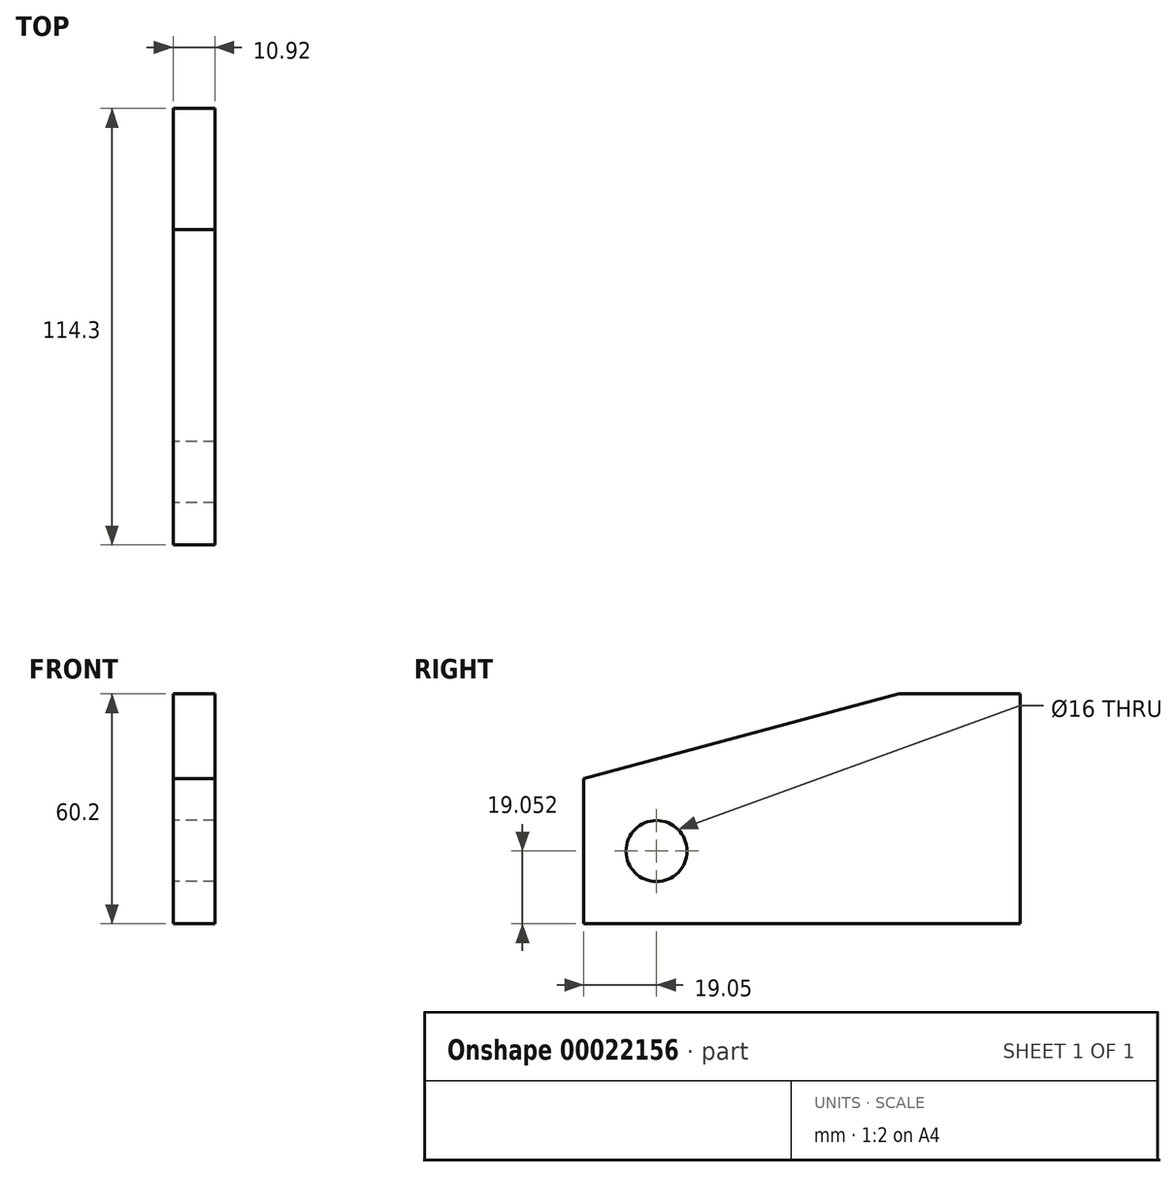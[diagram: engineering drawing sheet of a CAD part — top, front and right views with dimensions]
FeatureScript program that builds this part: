
annotation { "Feature Type Name" : "Feature", "Feature Type Description" : "" }
export const myFeature = defineFeature(function(context is Context, id is Id, definition is map)
    precondition{}
    {
        {
            var Q0;
            Q0=qCreatedBy(makeId("Right.planeOp"),FACE);
            var sketch = newSketch(context, id + "F0", { "sketchPlane" : qUnion([Q0])});
            skLineSegment(sketch, "E0.bottom", {"start": v(82.55, 0) * mm, "end": v(114.3, 0) * mm});
            skLineSegment(sketch, "E0.top", {"start": v(0, -60.2) * mm, "end": v(114.3, -60.2) * mm});
            skLineSegment(sketch, "E0.left", {"start": v(0, -22.12) * mm, "end": v(0, -60.2) * mm});
            skLineSegment(sketch, "E0.right", {"start": v(114.3, 0) * mm, "end": v(114.3, -60.2) * mm});
            skLineSegment(sketch, "E1", {"start": v(82.55, 0) * mm, "end": v(0, -22.12) * mm});
            skCircle(sketch, "E2", {"center": v(19.05, -41.15) * mm, "radius": 8 * mm});
            skSolve(sketch);
        }
        {
            var Q0;
            Q0 = qSketchRegion(id + "F0", true);
            extrude(context, id + "F1", {"entities" : qUnion([Q0]), "depth" : 10.92 * mm});
        }
    });
